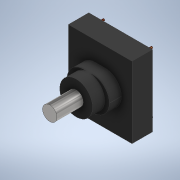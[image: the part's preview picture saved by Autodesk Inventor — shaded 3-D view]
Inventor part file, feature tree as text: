
AUTODESK INVENTOR PART (.ipt)
format: ipt  version: 2020 (Build 240168000, 168)  size: 160,256 bytes
history: native  units: mm
features: extrude x6, sketch x6, fillet x1
ambient origin geometry x8: Origin, YZ Plane, XZ Plane, XY Plane, X Axis, Y Axis, Z Axis, Center Point
bodies: Solid1 (feature_tree)
feature tree (13):
  extrude  "Extrusion1"  Depth=29.7mm
  extrude  "Extrusion2"  Depth=17.6mm
  fillet  "Fillet1"  Radius=13.7mm
  extrude  "Extrusion3"  Depth=6.8mm
  extrude  "Extrusion4"  Depth=5.0mm TaperAngle=0.0deg
  extrude  "Extrusion5"  Depth=11.0mm TaperAngle=0.0deg
  extrude  "Extrusion6"  Depth=4.0mm
  sketch  "Sketch1"  dims[d0=26.5mm d1=29.7mm]
  sketch  "Sketch2"  dims[d2=8.5mm d3=0.0mm d4=17.6mm d5=13.7mm]
  sketch  "Sketch3"  dims[d6=5.0mm d7=0.0mm d8=6.8mm]
  sketch  "Sketch4"  dims[d9=13.65mm d10=5.0mm d11=0.0mm]
  sketch  "Sketch5"  dims[d12=6.0mm d13=11.0mm d14=0.0mm]
  sketch  "Sketch6"  dims[d15=20.0mm d16=25.0mm d18=0.8mm d19=0.8mm d20=0.8mm d21=0.8mm d22=3.0mm d23=0.0mm d24=4.0mm d25=0.0mm]
